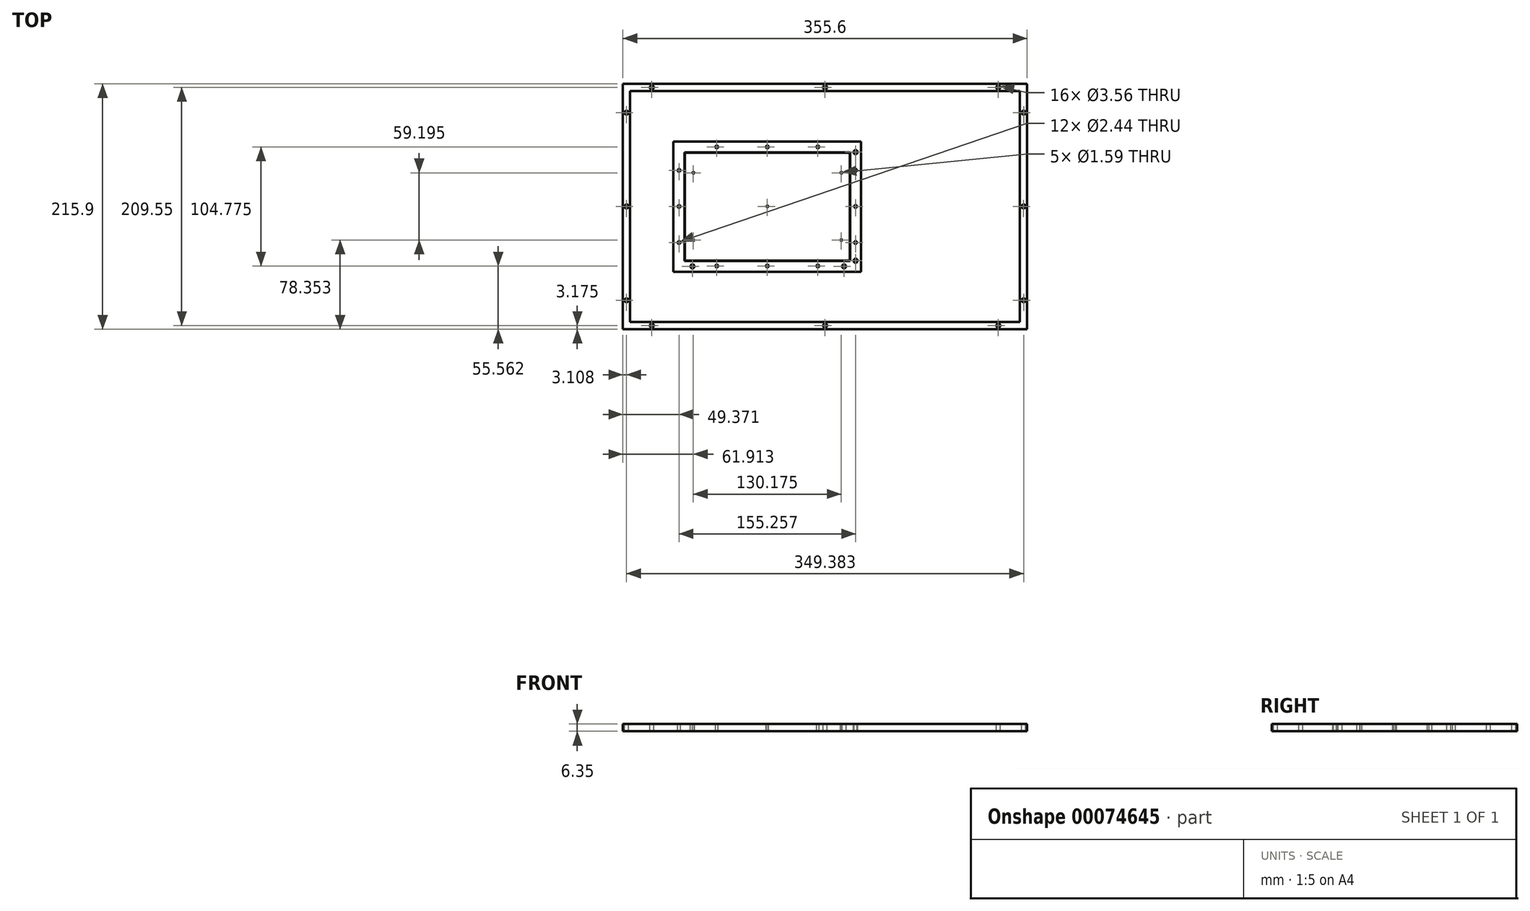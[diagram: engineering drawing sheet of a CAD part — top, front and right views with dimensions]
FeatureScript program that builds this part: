
annotation { "Feature Type Name" : "Feature", "Feature Type Description" : "" }
export const myFeature = defineFeature(function(context is Context, id is Id, definition is map)
    precondition{}
    {
        {
            var Q0;
            Q0=qCreatedBy(makeId("Top.planeOp"),FACE);
            var sketch = newSketch(context, id + "F0", { "sketchPlane" : qUnion([Q0])});
            skLineSegment(sketch, "E0.bottom", {"start": v(0, 0) * mm, "end": v(355.6, 0) * mm});
            skLineSegment(sketch, "E0.top", {"start": v(0, 215.9) * mm, "end": v(355.6, 215.9) * mm});
            skLineSegment(sketch, "E0.left", {"start": v(0, 0) * mm, "end": v(0, 215.9) * mm});
            skLineSegment(sketch, "E0.right", {"start": v(355.6, 0) * mm, "end": v(355.6, 215.9) * mm});
            skSolve(sketch);
        }
        {
            var Q0;
            Q0 = qSketchRegion(id + "F0", true);
            extrude(context, id + "F1", {"entities" : qUnion([Q0]), "depth" : 6.35 * mm});
        }
        {
            var Q0;
            Q0=makeQuery(id+"F1.opExtrude","CAP_FACE",FACE,{"disambiguationData":[OSD([sQuery(id+"F0.wireOp",EDGE,"E0.bottom"),sQuery(id+"F0.wireOp",EDGE,"E0.top"),sQuery(id+"F0.wireOp",EDGE,"E0.left"),sQuery(id+"F0.wireOp",EDGE,"E0.right")])],"isStart":false});
            var sketch = newSketch(context, id + "F2", { "sketchPlane" : qUnion([Q0])});
            skCircle(sketch, "E1", {"center": v(3.18, 107.95) * mm, "radius": 1.78 * mm});
            skLineSegment(sketch, "E2", {"start": v(177.8, 0) * mm, "end": v(177.8, 215.9) * mm, "construction": true});
            skLineSegment(sketch, "E3", {"start": v(355.6, 107.95) * mm, "end": v(0, 107.95) * mm, "construction": true});
            skCircle(sketch, "E4.1.0.0", {"center": v(3.1, 25.4) * mm, "radius": 1.78 * mm});
            skLineSegment(sketch, "E4.direction1", {"start": v(3.18, 107.95) * mm, "end": v(3.1, 25.4) * mm, "construction": true});
            skCircle(sketch, "E5.MirrorC", {"center": v(3.1, 190.5) * mm, "radius": 1.78 * mm});
            skCircle(sketch, "E6.1.0.0", {"center": v(177.8, 3.18) * mm, "radius": 1.78 * mm});
            skCircle(sketch, "E7.1.0.0", {"center": v(330.2, 3.18) * mm, "radius": 1.78 * mm});
            skLineSegment(sketch, "E7.direction1", {"start": v(177.8, 3.18) * mm, "end": v(330.2, 3.18) * mm, "construction": true});
            skCircle(sketch, "E8.MirrorC", {"center": v(330.2, 212.72) * mm, "radius": 1.78 * mm});
            skCircle(sketch, "E9.MirrorC", {"center": v(25.4, 3.18) * mm, "radius": 1.78 * mm});
            skCircle(sketch, "E10.MirrorC", {"center": v(177.8, 212.73) * mm, "radius": 1.78 * mm});
            skCircle(sketch, "E11.MirrorC", {"center": v(25.4, 212.72) * mm, "radius": 1.78 * mm});
            skCircle(sketch, "E12.MirrorC", {"center": v(352.5, 190.5) * mm, "radius": 1.78 * mm});
            skCircle(sketch, "E13.MirrorC", {"center": v(352.43, 107.95) * mm, "radius": 1.78 * mm});
            skCircle(sketch, "E14.MirrorC", {"center": v(352.5, 25.4) * mm, "radius": 1.78 * mm});
            skSolve(sketch);
        }
        {
            var Q0;
            Q0 = qSketchRegion(id + "F2", true);
            extrude(context, id + "F3", {"entities" : qUnion([Q0]), "operationType" : NewBodyOperationType.REMOVE, "endBound" : BoundingType.THROUGH_ALL, "oppositeDirection" : true, "depth" : 25.4 * mm});
        }
        {
            var Q0;
            Q0=makeQuery(id+"F1.opExtrude","CAP_FACE",FACE,{"disambiguationData":[OSD([sQuery(id+"F0.wireOp",EDGE,"E0.bottom"),sQuery(id+"F0.wireOp",EDGE,"E0.top"),sQuery(id+"F0.wireOp",EDGE,"E0.left"),sQuery(id+"F0.wireOp",EDGE,"E0.right")])],"isStart":false});
            var sketch = newSketch(context, id + "F4", { "sketchPlane" : qUnion([Q0])});
            skLineSegment(sketch, "E15", {"start": v(3.18, 107.95) * mm, "end": v(355.6, 107.95) * mm, "construction": true});
            skLineSegment(sketch, "E16", {"start": v(127, 25.7) * mm, "end": v(127, 181.73) * mm, "construction": true});
            skCircle(sketch, "E17", {"center": v(127, 107.95) * mm, "radius": 0.8 * mm});
            skLineSegment(sketch, "E18.direction1", {"start": v(127, 107.95) * mm, "end": v(192.09, 107.95) * mm, "construction": true});
            skLineSegment(sketch, "E19", {"start": v(61.91, 107.95) * mm, "end": v(61.91, 78.35) * mm, "construction": true});
            skCircle(sketch, "E20", {"center": v(61.91, 78.35) * mm, "radius": 0.8 * mm});
            skCircle(sketch, "E21.MirrorC", {"center": v(192.09, 78.35) * mm, "radius": 0.8 * mm});
            skCircle(sketch, "E22.MirrorC", {"center": v(61.91, 137.55) * mm, "radius": 0.8 * mm});
            skCircle(sketch, "E23.MirrorC", {"center": v(192.09, 137.55) * mm, "radius": 0.8 * mm});
            skSolve(sketch);
        }
        {
            var Q0;
            Q0 = qSketchRegion(id + "F4", true);
            extrude(context, id + "F5", {"entities" : qUnion([Q0]), "operationType" : NewBodyOperationType.REMOVE, "endBound" : BoundingType.THROUGH_ALL, "oppositeDirection" : true, "depth" : 25.4 * mm});
        }
        {
            var Q0;
            Q0=makeQuery(id+"F1.opExtrude","CAP_FACE",FACE,{"disambiguationData":[OSD([sQuery(id+"F0.wireOp",EDGE,"E0.bottom"),sQuery(id+"F0.wireOp",EDGE,"E0.top"),sQuery(id+"F0.wireOp",EDGE,"E0.left"),sQuery(id+"F0.wireOp",EDGE,"E0.right")])],"isStart":false});
            var sketch = newSketch(context, id + "F6", { "sketchPlane" : qUnion([Q0])});
            skLineSegment(sketch, "E24", {"start": v(127, 107.95) * mm, "end": v(204.63, 107.95) * mm, "construction": true});
            skLineSegment(sketch, "E25", {"start": v(204.63, 107.95) * mm, "end": v(204.63, 155.73) * mm, "construction": true});
            skCircle(sketch, "E26", {"center": v(204.63, 155.73) * mm, "radius": 1.78 * mm});
            skCircle(sketch, "E27.MirrorC", {"center": v(204.63, 60.17) * mm, "radius": 1.78 * mm});
            skLineSegment(sketch, "E28", {"start": v(127, 107.95) * mm, "end": v(127, 55.25) * mm, "construction": true});
            skLineSegment(sketch, "E29", {"start": v(127, 55.25) * mm, "end": v(194.49, 55.25) * mm, "construction": true});
            skCircle(sketch, "E30", {"center": v(194.49, 55.25) * mm, "radius": 1.78 * mm});
            skLineSegment(sketch, "E31", {"start": v(204.63, 107.95) * mm, "end": v(204.63, 60.17) * mm, "construction": true});
            skLineSegment(sketch, "E32", {"start": v(194.49, 55.25) * mm, "end": v(194.49, 33.23) * mm, "construction": true});
            skLineSegment(sketch, "E33", {"start": v(127, 55.25) * mm, "end": v(61.14, 55.24) * mm, "construction": true});
            skCircle(sketch, "E34", {"center": v(61.14, 55.24) * mm, "radius": 1.78 * mm});
            skSolve(sketch);
        }
        {
            var Q0;
            Q0 = qSketchRegion(id + "F6", true);
            extrude(context, id + "F7", {"entities" : qUnion([Q0]), "operationType" : NewBodyOperationType.REMOVE, "endBound" : BoundingType.THROUGH_ALL, "oppositeDirection" : true, "depth" : 25.4 * mm});
        }
        {
            var Q0;
            Q0=makeQuery(id+"F1.opExtrude","CAP_FACE",FACE,{"disambiguationData":[OSD([sQuery(id+"F0.wireOp",EDGE,"E0.bottom"),sQuery(id+"F0.wireOp",EDGE,"E0.top"),sQuery(id+"F0.wireOp",EDGE,"E0.left"),sQuery(id+"F0.wireOp",EDGE,"E0.right")])],"isStart":false});
            var sketch = newSketch(context, id + "F8", { "sketchPlane" : qUnion([Q0])});
            skLineSegment(sketch, "E35", {"start": v(127, 107.95) * mm, "end": v(127, 55.56) * mm, "construction": true});
            skLineSegment(sketch, "E36", {"start": v(127, 107.95) * mm, "end": v(127, 160.34) * mm, "construction": true});
            skLineSegment(sketch, "E37", {"start": v(127, 160.34) * mm, "end": v(82.55, 160.34) * mm, "construction": true});
            skLineSegment(sketch, "E38", {"start": v(127, 160.34) * mm, "end": v(171.45, 160.34) * mm, "construction": true});
            skLineSegment(sketch, "E39", {"start": v(127, 107.95) * mm, "end": v(49.37, 107.95) * mm, "construction": true});
            skCircle(sketch, "E40", {"center": v(82.55, 160.34) * mm, "radius": 1.22 * mm});
            skCircle(sketch, "E41", {"center": v(127, 160.34) * mm, "radius": 1.22 * mm});
            skCircle(sketch, "E42", {"center": v(171.45, 160.34) * mm, "radius": 1.22 * mm});
            skCircle(sketch, "E43.MirrorC", {"center": v(82.55, 55.56) * mm, "radius": 1.22 * mm});
            skCircle(sketch, "E44.MirrorC", {"center": v(127, 55.56) * mm, "radius": 1.22 * mm});
            skCircle(sketch, "E45.MirrorC", {"center": v(171.45, 55.56) * mm, "radius": 1.22 * mm});
            skCircle(sketch, "E46", {"center": v(204.63, 139.7) * mm, "radius": 1.22 * mm});
            skCircle(sketch, "E47.MirrorC", {"center": v(204.63, 76.2) * mm, "radius": 1.22 * mm});
            skLineSegment(sketch, "E48", {"start": v(204.63, 139.7) * mm, "end": v(204.63, 76.2) * mm, "construction": true});
            skCircle(sketch, "E49", {"center": v(204.63, 107.95) * mm, "radius": 1.22 * mm});
            skCircle(sketch, "E50.MirrorC", {"center": v(49.37, 139.7) * mm, "radius": 1.22 * mm});
            skCircle(sketch, "E51.MirrorC", {"center": v(49.37, 107.95) * mm, "radius": 1.22 * mm});
            skCircle(sketch, "E52.MirrorC", {"center": v(49.37, 76.2) * mm, "radius": 1.22 * mm});
            skLineSegment(sketch, "E53", {"start": v(49.37, 139.7) * mm, "end": v(204.63, 139.7) * mm, "construction": true});
            skLineSegment(sketch, "E54", {"start": v(204.63, 76.2) * mm, "end": v(49.37, 76.2) * mm, "construction": true});
            skLineSegment(sketch, "E55", {"start": v(49.37, 76.2) * mm, "end": v(49.37, 139.7) * mm, "construction": true});
            skSolve(sketch);
        }
        {
            var Q0;
            Q0 = qSketchRegion(id + "F8", true);
            extrude(context, id + "F9", {"entities" : qUnion([Q0]), "operationType" : NewBodyOperationType.REMOVE, "endBound" : BoundingType.THROUGH_ALL, "oppositeDirection" : true, "depth" : 25.4 * mm});
        }
        {
            var Q0;
            Q0=makeQuery(id+"F1.opExtrude","CAP_FACE",FACE,{"disambiguationData":[OSD([sQuery(id+"F0.wireOp",EDGE,"E0.bottom"),sQuery(id+"F0.wireOp",EDGE,"E0.top"),sQuery(id+"F0.wireOp",EDGE,"E0.left"),sQuery(id+"F0.wireOp",EDGE,"E0.right")])],"isStart":false});
            var sketch = newSketch(context, id + "F10", { "sketchPlane" : qUnion([Q0])});
            skLineSegment(sketch, "E56", {"start": v(49.37, 160.34) * mm, "end": v(49.37, 55.24) * mm, "construction": true});
            skLineSegment(sketch, "E57", {"start": v(127, 107.95) * mm, "end": v(127, 161.56) * mm, "construction": true});
            skLineSegment(sketch, "E58", {"start": v(204.63, 160.34) * mm, "end": v(204.63, 55.24) * mm, "construction": true});
            skLineSegment(sketch, "E59", {"start": v(49.37, 160.34) * mm, "end": v(204.63, 160.34) * mm, "construction": true});
            skLineSegment(sketch, "E60", {"start": v(127, 107.95) * mm, "end": v(220.94, 107.95) * mm, "construction": true});
            skLineSegment(sketch, "E61", {"start": v(49.37, 55.24) * mm, "end": v(204.63, 55.24) * mm, "construction": true});
            skPoint(sketch, "E62.orphan", {"position": v(49.37, 139.7) * mm});
            skPoint(sketch, "E63.orphan", {"position": v(82.55, 160.34) * mm});
            skPoint(sketch, "E64.orphan", {"position": v(204.63, 155.73) * mm});
            skPoint(sketch, "E65.orphan", {"position": v(61.14, 55.24) * mm});
            skLineSegment(sketch, "E66.0", {"start": v(44.44, 165.21) * mm, "end": v(209.56, 165.21) * mm});
            skLineSegment(sketch, "E67.0", {"start": v(6.35, 209.55) * mm, "end": v(6.35, 6.35) * mm});
            skLineSegment(sketch, "E67.1", {"start": v(349.25, 209.55) * mm, "end": v(6.35, 209.55) * mm});
            skLineSegment(sketch, "E67.2", {"start": v(349.25, 6.35) * mm, "end": v(349.25, 209.55) * mm});
            skLineSegment(sketch, "E67.3", {"start": v(6.35, 6.35) * mm, "end": v(349.25, 6.35) * mm});
            skLineSegment(sketch, "E68.0", {"start": v(44.44, 50.37) * mm, "end": v(209.56, 50.37) * mm});
            skLineSegment(sketch, "E69.0", {"start": v(209.23, 164.93) * mm, "end": v(209.23, 50.65) * mm});
            skLineSegment(sketch, "E70.0", {"start": v(44.77, 164.93) * mm, "end": v(44.77, 50.65) * mm});
            skLineSegment(sketch, "E71.0", {"start": v(44.44, 165.21) * mm, "end": v(44.44, 50.37) * mm});
            skLineSegment(sketch, "E72.0", {"start": v(209.56, 165.21) * mm, "end": v(209.56, 50.37) * mm});
            skLineSegment(sketch, "E73.0", {"start": v(44.77, 164.93) * mm, "end": v(209.23, 164.93) * mm});
            skLineSegment(sketch, "E74.0", {"start": v(44.77, 50.65) * mm, "end": v(209.23, 50.65) * mm});
            skLineSegment(sketch, "E75.0", {"start": v(54.13, 155.58) * mm, "end": v(199.87, 155.58) * mm});
            skLineSegment(sketch, "E75.1", {"start": v(54.13, 155.58) * mm, "end": v(54.13, 60) * mm});
            skLineSegment(sketch, "E75.2", {"start": v(54.13, 60) * mm, "end": v(199.87, 60) * mm});
            skLineSegment(sketch, "E75.3", {"start": v(199.87, 155.58) * mm, "end": v(199.87, 60) * mm});
            skLineSegment(sketch, "E76.0", {"start": v(54.41, 155.3) * mm, "end": v(199.59, 155.3) * mm});
            skLineSegment(sketch, "E76.1", {"start": v(54.41, 155.3) * mm, "end": v(54.41, 60.29) * mm});
            skLineSegment(sketch, "E76.2", {"start": v(54.41, 60.29) * mm, "end": v(199.59, 60.29) * mm});
            skLineSegment(sketch, "E76.3", {"start": v(199.59, 155.3) * mm, "end": v(199.59, 60.29) * mm});
            skSolve(sketch);
        }
        {
            var Q0;
            Q0 = qSketchRegion(id + "F10", true);
            var Q1;
            Q1=makeQuery(id+"F10.imprint","IMPRINT",FACE,{"disambiguationData":[TD([[makeQuery(id+"F10.imprint","IMPRINT",EDGE,{"derivedFrom":sQuery(id+"F10.wireOp",EDGE,"E75.0")}),-1.0]])]});
            extrude(context, id + "F11", {"entities" : qUnion([Q0, Q1]), "operationType" : NewBodyOperationType.REMOVE, "oppositeDirection" : true, "depth" : 0.28 * mm});
        }
    });
